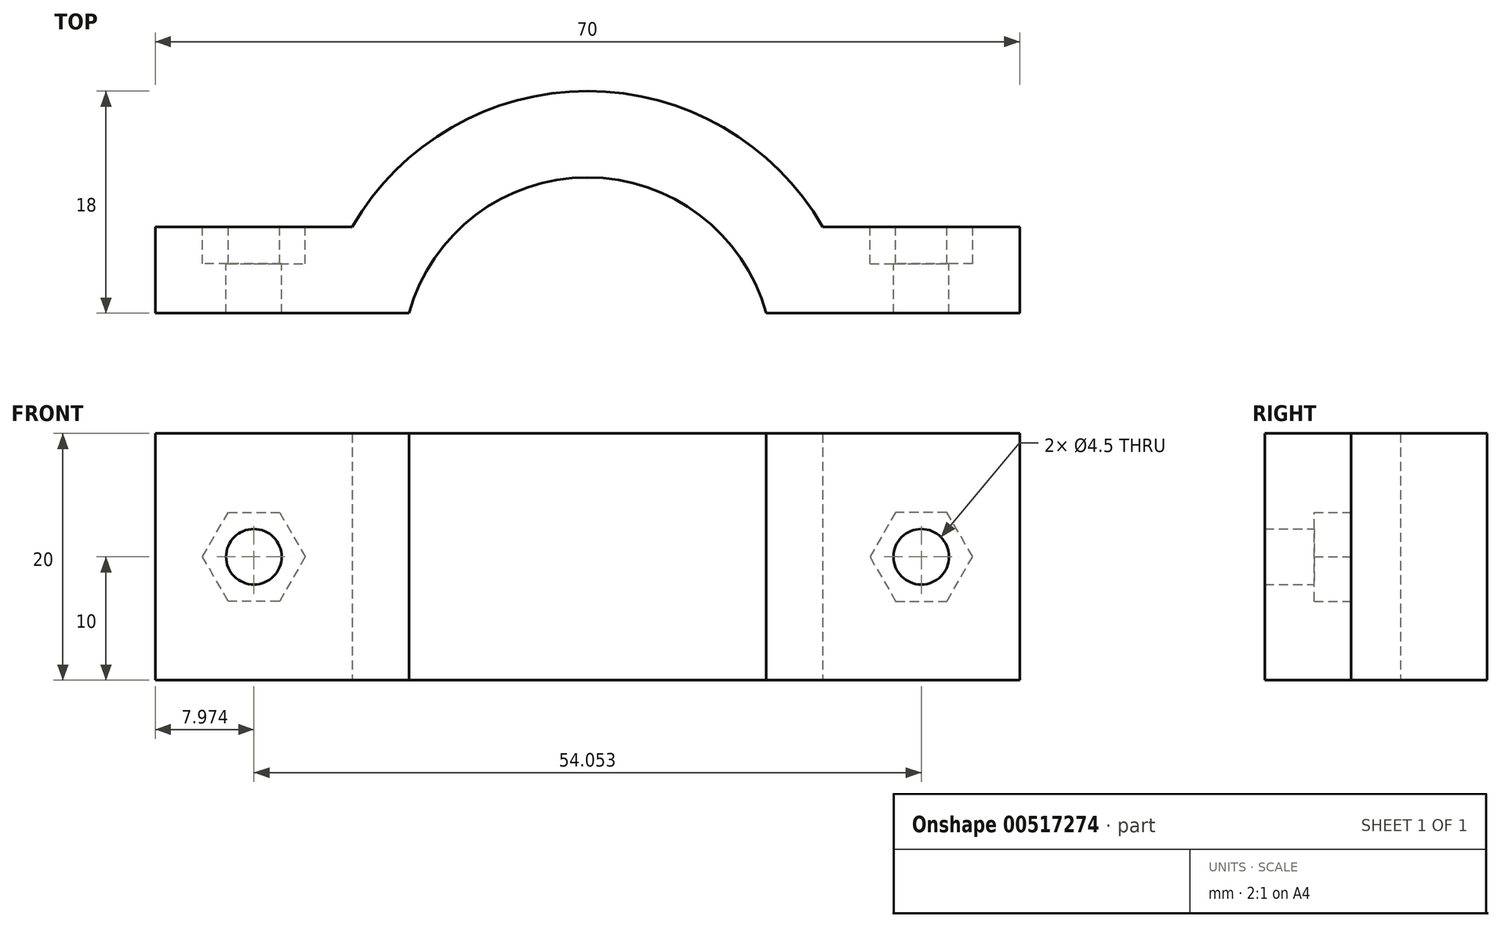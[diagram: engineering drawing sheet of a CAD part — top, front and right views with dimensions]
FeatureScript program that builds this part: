
annotation { "Feature Type Name" : "Feature", "Feature Type Description" : "" }
export const myFeature = defineFeature(function(context is Context, id is Id, definition is map)
    precondition{}
    {
        {
            var Q0;
            Q0=qCreatedBy(makeId("Top.planeOp"),FACE);
            var sketch = newSketch(context, id + "F0", { "sketchPlane" : qUnion([Q0])});
            skLineSegment(sketch, "E0", {"start": v(-35, 0) * mm, "end": v(-14.46, 0) * mm});
            skLineSegment(sketch, "E1.MirrorCS", {"start": v(35, 0) * mm, "end": v(14.46, 0) * mm});
            skArc(sketch, "E2", {"start": v(14.46, 0) * mm, "mid": v(0, 11) * mm, "end": v(-14.46, 0) * mm});
            skArc(sketch, "E3.0", {"start": v(19.05, 7) * mm, "mid": v(0, 18) * mm, "end": v(-19.05, 7) * mm});
            skLineSegment(sketch, "E4.0", {"start": v(-35, 7) * mm, "end": v(-19.05, 7) * mm});
            skLineSegment(sketch, "E5.MirrorCS", {"start": v(35, 7) * mm, "end": v(19.05, 7) * mm});
            skLineSegment(sketch, "E6.MirrorCS", {"start": v(35, 7) * mm, "end": v(35, 0) * mm});
            skLineSegment(sketch, "E7", {"start": v(-35, 7) * mm, "end": v(-35, 0) * mm});
            skSolve(sketch);
        }
        {
            var Q0;
            Q0=qSketchRegion(id+"F0",true);
            extrude(context, id + "F1", {"entities" : qUnion([Q0]), "endBound" : BoundingType.SYMMETRIC, "depth" : 20 * mm, "offsetDistance" : 25 * mm});
        }
        {
            var Q0;
            Q0=makeQuery(id+"F1.opExtrude","SWEPT_FACE",FACE,{"disambiguationData":[OSD([sQuery(id+"F0.wireOp",EDGE,"E5.MirrorCS")])]});
            var sketch = newSketch(context, id + "F2", { "sketchPlane" : qUnion([Q0])});
            skCircle(sketch, "E8", {"center": v(-27.03, 0) * mm, "radius": 2.25 * mm});
            skLineSegment(sketch, "E9", {"start": v(-27.03, 10) * mm, "end": v(-27.03, -10) * mm, "construction": true});
            skCircle(sketch, "E10.MirrorC", {"center": v(27.03, 0) * mm, "radius": 2.25 * mm});
            skSolve(sketch);
        }
        {
            var Q0;
            Q0=qSketchRegion(id+"F2",true);
            extrude(context, id + "F3", {"entities" : qUnion([Q0]), "operationType" : NewBodyOperationType.REMOVE, "oppositeDirection" : true, "depth" : 25 * mm, "offsetDistance" : 25 * mm});
        }
        {
            var Q0;
            Q0=makeQuery(id+"F1.opExtrude","SWEPT_FACE",FACE,{"disambiguationData":[OSD([sQuery(id+"F0.wireOp",EDGE,"E5.MirrorCS")])]});
            var sketch = newSketch(context, id + "F4", { "sketchPlane" : qUnion([Q0])});
            skCircle(sketch, "E11.0", {"center": v(-27.03, 0) * mm, "radius": 2.25 * mm});
            skCircle(sketch, "E12.cCircle", {"center": v(-27.03, 0) * mm, "radius": 3.6 * mm, "construction": true});
            skLineSegment(sketch, "E12.0", {"start": v(-31.18, 0) * mm, "end": v(-29.1, 3.6) * mm});
            skLineSegment(sketch, "E12.1", {"start": v(-29.1, 3.6) * mm, "end": v(-24.95, 3.6) * mm});
            skLineSegment(sketch, "E12.2", {"start": v(-24.95, 3.6) * mm, "end": v(-22.87, 0) * mm});
            skLineSegment(sketch, "E12.3", {"start": v(-22.87, 0) * mm, "end": v(-24.95, -3.6) * mm});
            skLineSegment(sketch, "E12.4", {"start": v(-24.95, -3.6) * mm, "end": v(-29.1, -3.6) * mm});
            skLineSegment(sketch, "E12.5", {"start": v(-29.1, -3.6) * mm, "end": v(-31.18, 0) * mm});
            skPoint(sketch, "E12.0.midPoint", {"position": v(-30.14, 1.8) * mm});
            skLineSegment(sketch, "E13.MirrorCS", {"start": v(31.18, 0) * mm, "end": v(29.1, 3.6) * mm});
            skLineSegment(sketch, "E14.MirrorCS", {"start": v(29.1, 3.6) * mm, "end": v(24.95, 3.6) * mm});
            skLineSegment(sketch, "E15.MirrorCS", {"start": v(24.95, 3.6) * mm, "end": v(22.87, 0) * mm});
            skLineSegment(sketch, "E16.MirrorCS", {"start": v(22.87, 0) * mm, "end": v(24.95, -3.6) * mm});
            skPoint(sketch, "E17.MirrorP", {"position": v(30.14, 1.8) * mm});
            skCircle(sketch, "E18.MirrorC", {"center": v(27.03, 0) * mm, "radius": 3.6 * mm, "construction": true});
            skLineSegment(sketch, "E19.MirrorCS", {"start": v(24.95, -3.6) * mm, "end": v(29.1, -3.6) * mm});
            skLineSegment(sketch, "E20.MirrorCS", {"start": v(29.1, -3.6) * mm, "end": v(31.18, 0) * mm});
            skSolve(sketch);
        }
        {
            var Q0;
            Q0=qSketchRegion(id+"F4",true);
            extrude(context, id + "F5", {"entities" : qUnion([Q0]), "operationType" : NewBodyOperationType.REMOVE, "oppositeDirection" : true, "depth" : 3 * mm, "offsetDistance" : 25 * mm});
        }
    });
